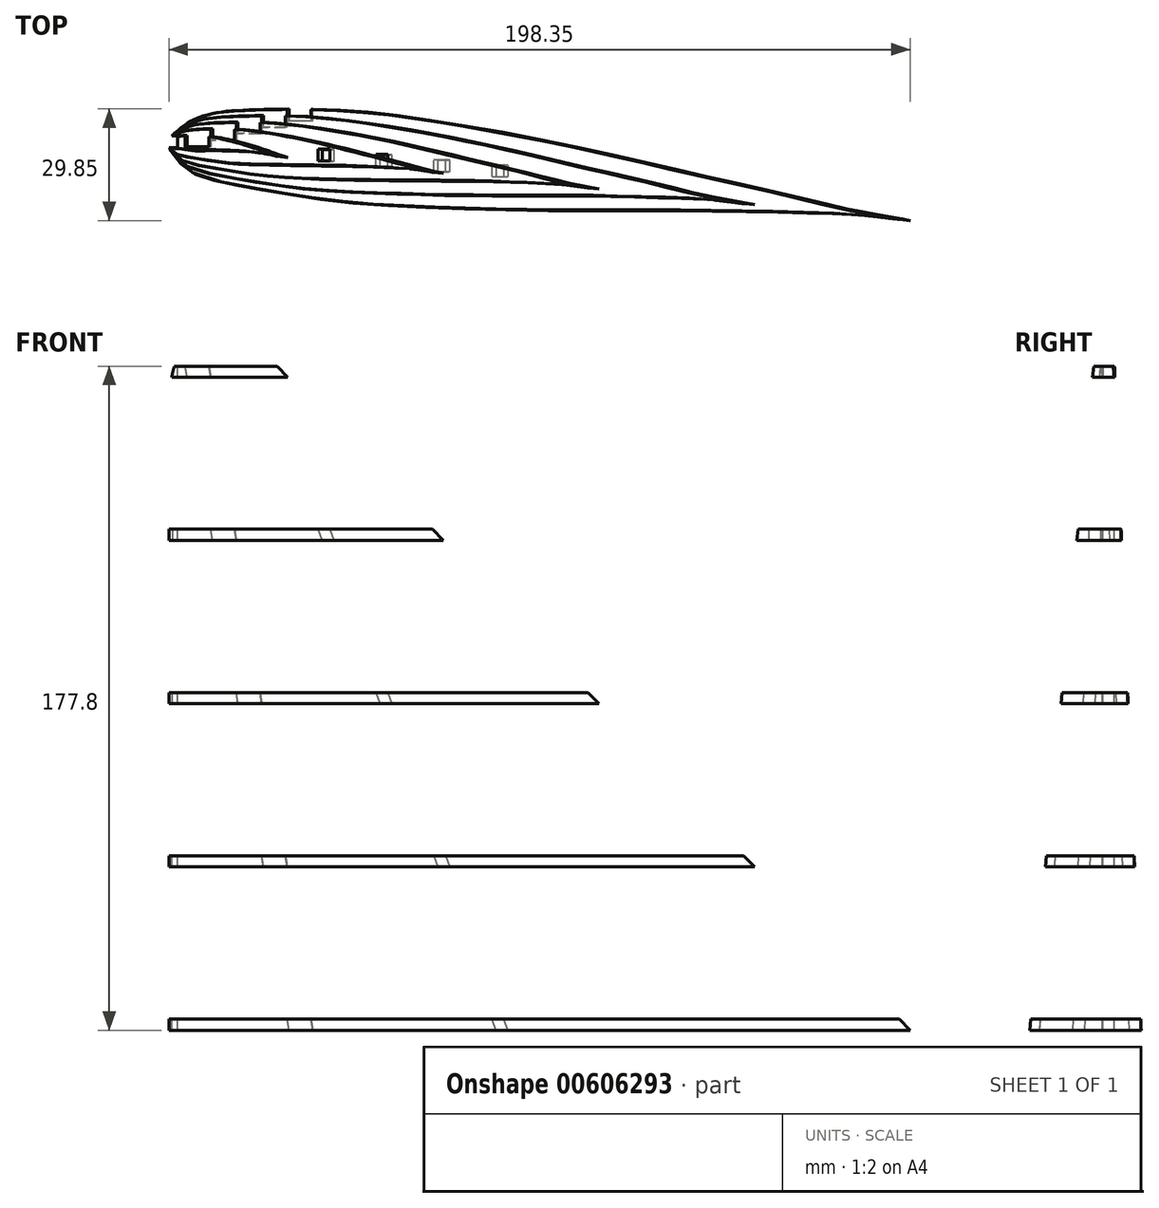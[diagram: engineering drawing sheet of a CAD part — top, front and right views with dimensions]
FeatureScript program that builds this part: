
annotation { "Feature Type Name" : "Feature", "Feature Type Description" : "" }
export const myFeature = defineFeature(function(context is Context, id is Id, definition is map)
    precondition{}
    {
        {
            var Q0;
            Q0=qCreatedBy(makeId("Top.planeOp"),FACE);
            var sketch = newSketch(context, id + "F0", { "sketchPlane" : qUnion([Q0])});
            skLineSegment(sketch, "E0", {"start": v(0, 0) * mm, "end": v(2.33, 2.26) * mm});
            skLineSegment(sketch, "E1", {"start": v(2.33, 2.26) * mm, "end": v(3.53, 3.33) * mm});
            skLineSegment(sketch, "E2", {"start": v(3.53, 3.33) * mm, "end": v(4.77, 4.31) * mm});
            skLineSegment(sketch, "E3", {"start": v(4.77, 4.31) * mm, "end": v(6.35, 5.36) * mm});
            skLineSegment(sketch, "E4", {"start": v(6.35, 5.36) * mm, "end": v(7.43, 5.94) * mm});
            skLineSegment(sketch, "E5", {"start": v(7.43, 5.94) * mm, "end": v(8.86, 6.56) * mm});
            skLineSegment(sketch, "E6", {"start": v(8.86, 6.56) * mm, "end": v(10.34, 7.07) * mm});
            skLineSegment(sketch, "E7", {"start": v(10.34, 7.07) * mm, "end": v(11.88, 7.48) * mm});
            skLineSegment(sketch, "E8", {"start": v(11.88, 7.48) * mm, "end": v(13.45, 7.8) * mm});
            skLineSegment(sketch, "E9", {"start": v(13.45, 7.8) * mm, "end": v(16.68, 8.22) * mm});
            skLineSegment(sketch, "E10", {"start": v(16.68, 8.22) * mm, "end": v(19.98, 8.45) * mm});
            skLineSegment(sketch, "E11", {"start": v(19.98, 8.45) * mm, "end": v(22.04, 8.54) * mm});
            skLineSegment(sketch, "E12", {"start": v(22.04, 8.54) * mm, "end": v(29.75, 8.77) * mm});
            skLineSegment(sketch, "E13", {"start": v(29.75, 8.77) * mm, "end": v(36.12, 8.82) * mm});
            skLineSegment(sketch, "E14", {"start": v(36.12, 8.82) * mm, "end": v(42.43, 8.7) * mm});
            skLineSegment(sketch, "E15", {"start": v(42.43, 8.7) * mm, "end": v(46.07, 8.54) * mm});
            skLineSegment(sketch, "E16", {"start": v(46.07, 8.54) * mm, "end": v(55.05, 7.84) * mm});
            skLineSegment(sketch, "E17", {"start": v(55.05, 7.84) * mm, "end": v(61.4, 7.12) * mm});
            skLineSegment(sketch, "E18", {"start": v(61.4, 7.12) * mm, "end": v(67.74, 6.27) * mm});
            skLineSegment(sketch, "E19", {"start": v(67.74, 6.27) * mm, "end": v(76.25, 4.96) * mm});
            skLineSegment(sketch, "E20", {"start": v(76.25, 4.96) * mm, "end": v(86.73, 3.2) * mm});
            skLineSegment(sketch, "E21", {"start": v(86.73, 3.2) * mm, "end": v(99.29, 0.84) * mm});
            skLineSegment(sketch, "E22", {"start": v(99.29, 0.84) * mm, "end": v(109.21, -1.2) * mm});
            skLineSegment(sketch, "E23", {"start": v(109.21, -1.2) * mm, "end": v(123.98, -4.49) * mm});
            skLineSegment(sketch, "E24", {"start": v(123.98, -4.49) * mm, "end": v(130.17, -5.92) * mm});
            skLineSegment(sketch, "E25", {"start": v(130.17, -5.92) * mm, "end": v(136.44, -7.38) * mm});
            skLineSegment(sketch, "E26", {"start": v(136.44, -7.38) * mm, "end": v(142.37, -8.74) * mm});
            skLineSegment(sketch, "E27", {"start": v(142.37, -8.74) * mm, "end": v(149.34, -10.3) * mm});
            skLineSegment(sketch, "E28", {"start": v(149.34, -10.3) * mm, "end": v(155.82, -11.75) * mm});
            skLineSegment(sketch, "E29", {"start": v(155.82, -11.75) * mm, "end": v(162.12, -13.17) * mm});
            skLineSegment(sketch, "E30", {"start": v(162.12, -13.17) * mm, "end": v(165.14, -13.87) * mm});
            skLineSegment(sketch, "E31", {"start": v(165.14, -13.87) * mm, "end": v(168.06, -14.55) * mm});
            skLineSegment(sketch, "E32", {"start": v(168.06, -14.55) * mm, "end": v(171.17, -15.29) * mm});
            skLineSegment(sketch, "E33", {"start": v(171.17, -15.29) * mm, "end": v(173.51, -15.86) * mm});
            skLineSegment(sketch, "E34", {"start": v(173.51, -15.86) * mm, "end": v(176.14, -16.5) * mm});
            skLineSegment(sketch, "E35", {"start": v(176.14, -16.5) * mm, "end": v(178.86, -17.16) * mm});
            skLineSegment(sketch, "E36", {"start": v(178.86, -17.16) * mm, "end": v(181.8, -17.82) * mm});
            skLineSegment(sketch, "E37", {"start": v(181.8, -17.82) * mm, "end": v(183.4, -18.16) * mm});
            skLineSegment(sketch, "E38", {"start": v(183.4, -18.16) * mm, "end": v(185.1, -18.5) * mm});
            skLineSegment(sketch, "E39", {"start": v(185.1, -18.5) * mm, "end": v(186.92, -18.87) * mm});
            skLineSegment(sketch, "E40", {"start": v(186.92, -18.87) * mm, "end": v(188.88, -19.24) * mm});
            skLineSegment(sketch, "E41", {"start": v(188.88, -19.24) * mm, "end": v(191.22, -19.66) * mm});
            skLineSegment(sketch, "E42", {"start": v(191.22, -19.66) * mm, "end": v(193.25, -20.01) * mm});
            skLineSegment(sketch, "E43", {"start": v(193.25, -20.01) * mm, "end": v(195.45, -20.38) * mm});
            skLineSegment(sketch, "E44", {"start": v(195.45, -20.38) * mm, "end": v(196.45, -20.55) * mm});
            skLineSegment(sketch, "E45", {"start": v(196.45, -20.55) * mm, "end": v(197.34, -20.7) * mm});
            skLineSegment(sketch, "E46", {"start": v(197.34, -20.7) * mm, "end": v(198.1, -20.83) * mm});
            skLineSegment(sketch, "E47", {"start": v(198.1, -20.83) * mm, "end": v(198.67, -20.94) * mm});
            skLineSegment(sketch, "E48", {"start": v(198.67, -20.94) * mm, "end": v(199.04, -21) * mm});
            skLineSegment(sketch, "E49", {"start": v(199.04, -21) * mm, "end": v(199.17, -21.05) * mm});
            skLineSegment(sketch, "E50", {"start": v(199.17, -21.05) * mm, "end": v(199.05, -21.04) * mm});
            skLineSegment(sketch, "E51", {"start": v(199.05, -21.04) * mm, "end": v(198.67, -21) * mm});
            skLineSegment(sketch, "E52", {"start": v(198.67, -21) * mm, "end": v(198.08, -20.93) * mm});
            skLineSegment(sketch, "E53", {"start": v(198.08, -20.93) * mm, "end": v(197.31, -20.84) * mm});
            skLineSegment(sketch, "E54", {"start": v(197.31, -20.84) * mm, "end": v(196.4, -20.72) * mm});
            skLineSegment(sketch, "E55", {"start": v(196.4, -20.72) * mm, "end": v(195.4, -20.6) * mm});
            skLineSegment(sketch, "E56", {"start": v(195.4, -20.6) * mm, "end": v(192.61, -20.25) * mm});
            skLineSegment(sketch, "E57", {"start": v(192.61, -20.25) * mm, "end": v(191.14, -20.09) * mm});
            skLineSegment(sketch, "E58", {"start": v(191.14, -20.09) * mm, "end": v(189.16, -19.88) * mm});
            skLineSegment(sketch, "E59", {"start": v(189.16, -19.88) * mm, "end": v(187.3, -19.7) * mm});
            skLineSegment(sketch, "E60", {"start": v(187.3, -19.7) * mm, "end": v(185.56, -19.56) * mm});
            skLineSegment(sketch, "E61", {"start": v(185.56, -19.56) * mm, "end": v(183.9, -19.44) * mm});
            skLineSegment(sketch, "E62", {"start": v(183.9, -19.44) * mm, "end": v(182.34, -19.35) * mm});
            skLineSegment(sketch, "E63", {"start": v(182.34, -19.35) * mm, "end": v(179.38, -19.22) * mm});
            skLineSegment(sketch, "E64", {"start": v(179.38, -19.22) * mm, "end": v(172.56, -19.06) * mm});
            skLineSegment(sketch, "E65", {"start": v(172.56, -19.06) * mm, "end": v(170.97, -19.03) * mm});
            skLineSegment(sketch, "E66", {"start": v(170.97, -19.03) * mm, "end": v(168, -18.97) * mm});
            skLineSegment(sketch, "E67", {"start": v(168, -18.97) * mm, "end": v(164.94, -18.9) * mm});
            skLineSegment(sketch, "E68", {"start": v(164.94, -18.9) * mm, "end": v(161.8, -18.83) * mm});
            skLineSegment(sketch, "E69", {"start": v(161.8, -18.83) * mm, "end": v(155.31, -18.68) * mm});
            skLineSegment(sketch, "E70", {"start": v(155.31, -18.68) * mm, "end": v(148.7, -18.55) * mm});
            skLineSegment(sketch, "E71", {"start": v(148.7, -18.55) * mm, "end": v(142.57, -18.47) * mm});
            skLineSegment(sketch, "E72", {"start": v(142.57, -18.47) * mm, "end": v(135.55, -18.43) * mm});
            skLineSegment(sketch, "E73", {"start": v(135.55, -18.43) * mm, "end": v(122.78, -18.45) * mm});
            skLineSegment(sketch, "E74", {"start": v(122.78, -18.45) * mm, "end": v(107.63, -18.47) * mm});
            skLineSegment(sketch, "E75", {"start": v(107.63, -18.47) * mm, "end": v(97.5, -18.36) * mm});
            skLineSegment(sketch, "E76", {"start": v(97.5, -18.36) * mm, "end": v(84.74, -18.06) * mm});
            skLineSegment(sketch, "E77", {"start": v(84.74, -18.06) * mm, "end": v(72.88, -17.67) * mm});
            skLineSegment(sketch, "E78", {"start": v(72.88, -17.67) * mm, "end": v(59.08, -17.03) * mm});
            skLineSegment(sketch, "E79", {"start": v(59.08, -17.03) * mm, "end": v(52.7, -16.59) * mm});
            skLineSegment(sketch, "E80", {"start": v(52.7, -16.59) * mm, "end": v(46.4, -16) * mm});
            skLineSegment(sketch, "E81", {"start": v(46.4, -16) * mm, "end": v(42.1, -15.49) * mm});
            skLineSegment(sketch, "E82", {"start": v(42.1, -15.49) * mm, "end": v(33.97, -14.26) * mm});
            skLineSegment(sketch, "E83", {"start": v(33.97, -14.26) * mm, "end": v(27.74, -13.17) * mm});
            skLineSegment(sketch, "E84", {"start": v(27.74, -13.17) * mm, "end": v(18.67, -11.52) * mm});
            skLineSegment(sketch, "E85", {"start": v(18.67, -11.52) * mm, "end": v(14.77, -10.79) * mm});
            skLineSegment(sketch, "E86", {"start": v(14.77, -10.79) * mm, "end": v(11.53, -10) * mm});
            skLineSegment(sketch, "E87", {"start": v(11.53, -10) * mm, "end": v(9.97, -9.52) * mm});
            skLineSegment(sketch, "E88", {"start": v(9.97, -9.52) * mm, "end": v(8.48, -8.94) * mm});
            skLineSegment(sketch, "E89", {"start": v(8.48, -8.94) * mm, "end": v(7.07, -8.26) * mm});
            skLineSegment(sketch, "E90", {"start": v(7.07, -8.26) * mm, "end": v(5.75, -7.45) * mm});
            skLineSegment(sketch, "E91", {"start": v(5.75, -7.45) * mm, "end": v(4.17, -6.16) * mm});
            skLineSegment(sketch, "E92", {"start": v(4.17, -6.16) * mm, "end": v(3.47, -5.41) * mm});
            skLineSegment(sketch, "E93", {"start": v(3.47, -5.41) * mm, "end": v(2.5, -4.18) * mm});
            skLineSegment(sketch, "E94", {"start": v(2.5, -4.18) * mm, "end": v(1.62, -2.84) * mm});
            skLineSegment(sketch, "E95", {"start": v(1.62, -2.84) * mm, "end": v(0, 0) * mm});
            skSolve(sketch);
        }
        {
            var Q0;
            Q0=qCreatedBy(makeId("Top.planeOp"),FACE);
            var sketch = newSketch(context, id + "F1", { "sketchPlane" : qUnion([Q0])});
            skPoint(sketch, "E96.0", {"position": v(0, 0) * mm});
            skPoint(sketch, "E96.1", {"position": v(3.53, 3.33) * mm});
            skPoint(sketch, "E96.2", {"position": v(7.43, 5.94) * mm});
            skPoint(sketch, "E96.3", {"position": v(13.45, 7.8) * mm});
            skPoint(sketch, "E96.4", {"position": v(22.04, 8.54) * mm});
            skPoint(sketch, "E96.5", {"position": v(42.43, 8.7) * mm});
            skPoint(sketch, "E96.6", {"position": v(67.74, 6.27) * mm});
            skPoint(sketch, "E96.7", {"position": v(109.21, -1.2) * mm});
            skPoint(sketch, "E96.8", {"position": v(142.37, -8.74) * mm});
            skPoint(sketch, "E96.9", {"position": v(165.14, -13.87) * mm});
            skPoint(sketch, "E96.10", {"position": v(178.86, -17.16) * mm});
            skPoint(sketch, "E96.11", {"position": v(186.92, -18.87) * mm});
            skPoint(sketch, "E96.12", {"position": v(193.25, -20.01) * mm});
            skPoint(sketch, "E96.13", {"position": v(197.34, -20.7) * mm});
            skPoint(sketch, "E96.14", {"position": v(199.17, -21.05) * mm});
            skPoint(sketch, "E97.0", {"position": v(2.5, -4.18) * mm});
            skPoint(sketch, "E97.1", {"position": v(7.07, -8.26) * mm});
            skPoint(sketch, "E97.2", {"position": v(14.77, -10.79) * mm});
            skPoint(sketch, "E97.3", {"position": v(27.74, -13.17) * mm});
            skPoint(sketch, "E97.4", {"position": v(46.4, -16) * mm});
            skPoint(sketch, "E97.5", {"position": v(72.88, -17.67) * mm});
            skPoint(sketch, "E97.6", {"position": v(107.63, -18.47) * mm});
            skPoint(sketch, "E97.7", {"position": v(142.57, -18.47) * mm});
            skPoint(sketch, "E97.8", {"position": v(164.94, -18.9) * mm});
            skPoint(sketch, "E97.9", {"position": v(179.38, -19.22) * mm});
            skPoint(sketch, "E97.10", {"position": v(185.56, -19.56) * mm});
            skPoint(sketch, "E97.11", {"position": v(191.14, -20.09) * mm});
            skPoint(sketch, "E97.12", {"position": v(195.4, -20.6) * mm});
            skFitSpline(sketch, "E98", {"points": [v(0, 0) * mm, v(3.53, 3.33) * mm, v(7.43, 5.94) * mm, v(13.45, 7.8) * mm, v(22.04, 8.54) * mm, v(42.43, 8.7) * mm, v(67.74, 6.27) * mm, v(109.21, -1.2) * mm, v(142.37, -8.74) * mm, v(165.14, -13.87) * mm, v(178.86, -17.16) * mm, v(186.92, -18.87) * mm, v(193.25, -20.01) * mm, v(197.34, -20.7) * mm, v(199.17, -21.05) * mm], "startDerivative": vector(77.94, 76.97) * mm, "endDerivative": vector(59.78, -11.65) * mm});
            skFitSpline(sketch, "E99", {"points": [v(0, 0) * mm, v(2.5, -4.18) * mm, v(7.07, -8.26) * mm, v(14.77, -10.79) * mm, v(27.74, -13.17) * mm, v(46.4, -16) * mm, v(72.88, -17.67) * mm, v(107.63, -18.47) * mm, v(142.57, -18.47) * mm, v(164.94, -18.9) * mm, v(179.38, -19.22) * mm, v(185.56, -19.56) * mm, v(191.14, -20.09) * mm, v(195.4, -20.6) * mm, v(199.17, -21.05) * mm], "startDerivative": vector(49.75, -95.35) * mm, "endDerivative": vector(95.8, -11.43) * mm});
            skSolve(sketch);
        }
        {
            var Q0;
            Q0=qCreatedBy(makeId("Top.planeOp"),FACE);
            cPlane(context, id + "F2", {"entities" : qUnion([Q0]), "cplaneType" : CPlaneType.OFFSET, "offset" : 177.8 * mm, "width" : 152.4 * mm, "height" : 152.4 * mm});
        }
        {
            var Q0;
            Q0=qCreatedBy(id+"F2.planeOp",FACE);
            var sketch = newSketch(context, id + "F3", { "sketchPlane" : qUnion([Q0])});
            skLineSegment(sketch, "E100", {"start": v(0, 0) * mm, "end": v(0.76, 0.6) * mm});
            skLineSegment(sketch, "E101", {"start": v(0.76, 0.6) * mm, "end": v(1.2, 0.87) * mm});
            skLineSegment(sketch, "E102", {"start": v(1.2, 0.87) * mm, "end": v(1.6, 1.06) * mm});
            skLineSegment(sketch, "E103", {"start": v(1.6, 1.06) * mm, "end": v(2.51, 1.33) * mm});
            skLineSegment(sketch, "E104", {"start": v(2.51, 1.33) * mm, "end": v(3.73, 1.52) * mm});
            skLineSegment(sketch, "E105", {"start": v(3.73, 1.52) * mm, "end": v(5.41, 1.66) * mm});
            skLineSegment(sketch, "E106", {"start": v(5.41, 1.66) * mm, "end": v(7.35, 1.7) * mm});
            skLineSegment(sketch, "E107", {"start": v(7.35, 1.7) * mm, "end": v(9.24, 1.62) * mm});
            skLineSegment(sketch, "E108", {"start": v(9.24, 1.62) * mm, "end": v(11.74, 1.34) * mm});
            skLineSegment(sketch, "E109", {"start": v(11.74, 1.34) * mm, "end": v(13.07, 1.13) * mm});
            skLineSegment(sketch, "E110", {"start": v(13.07, 1.13) * mm, "end": v(16.43, 0.42) * mm});
            skLineSegment(sketch, "E111", {"start": v(16.43, 0.42) * mm, "end": v(18.66, -0.16) * mm});
            skLineSegment(sketch, "E112", {"start": v(18.66, -0.16) * mm, "end": v(21.09, -0.87) * mm});
            skLineSegment(sketch, "E113", {"start": v(21.09, -0.87) * mm, "end": v(22.44, -1.3) * mm});
            skLineSegment(sketch, "E114", {"start": v(22.44, -1.3) * mm, "end": v(24.3, -1.92) * mm});
            skLineSegment(sketch, "E115", {"start": v(24.3, -1.92) * mm, "end": v(25.2, -2.24) * mm});
            skLineSegment(sketch, "E116", {"start": v(25.2, -2.24) * mm, "end": v(25.86, -2.48) * mm});
            skLineSegment(sketch, "E117", {"start": v(25.86, -2.48) * mm, "end": v(26.64, -2.77) * mm});
            skLineSegment(sketch, "E118", {"start": v(26.64, -2.77) * mm, "end": v(27.1, -2.93) * mm});
            skLineSegment(sketch, "E119", {"start": v(27.1, -2.93) * mm, "end": v(27.64, -3.13) * mm});
            skLineSegment(sketch, "E120", {"start": v(27.64, -3.13) * mm, "end": v(28.26, -3.35) * mm});
            skLineSegment(sketch, "E121", {"start": v(28.26, -3.35) * mm, "end": v(28.99, -3.6) * mm});
            skLineSegment(sketch, "E122", {"start": v(28.99, -3.6) * mm, "end": v(29.3, -3.71) * mm});
            skLineSegment(sketch, "E123", {"start": v(29.3, -3.71) * mm, "end": v(29.57, -3.8) * mm});
            skLineSegment(sketch, "E124", {"start": v(29.57, -3.8) * mm, "end": v(29.74, -3.87) * mm});
            skLineSegment(sketch, "E125", {"start": v(29.74, -3.87) * mm, "end": v(29.79, -3.9) * mm});
            skLineSegment(sketch, "E126", {"start": v(29.79, -3.9) * mm, "end": v(29.75, -3.88) * mm});
            skLineSegment(sketch, "E127", {"start": v(29.75, -3.88) * mm, "end": v(29.24, -3.73) * mm});
            skLineSegment(sketch, "E128", {"start": v(29.24, -3.73) * mm, "end": v(28.9, -3.64) * mm});
            skLineSegment(sketch, "E129", {"start": v(28.9, -3.64) * mm, "end": v(27.91, -3.4) * mm});
            skLineSegment(sketch, "E130", {"start": v(27.91, -3.4) * mm, "end": v(26.5, -3.14) * mm});
            skLineSegment(sketch, "E131", {"start": v(26.5, -3.14) * mm, "end": v(24.27, -2.81) * mm});
            skLineSegment(sketch, "E132", {"start": v(24.27, -2.81) * mm, "end": v(21.92, -2.54) * mm});
            skLineSegment(sketch, "E133", {"start": v(21.92, -2.54) * mm, "end": v(20.37, -2.4) * mm});
            skLineSegment(sketch, "E134", {"start": v(20.37, -2.4) * mm, "end": v(18.46, -2.28) * mm});
            skLineSegment(sketch, "E135", {"start": v(18.46, -2.28) * mm, "end": v(16.3, -2.18) * mm});
            skLineSegment(sketch, "E136", {"start": v(16.3, -2.18) * mm, "end": v(10.72, -2.1) * mm});
            skLineSegment(sketch, "E137", {"start": v(10.72, -2.1) * mm, "end": v(8.83, -2.14) * mm});
            skLineSegment(sketch, "E138", {"start": v(8.83, -2.14) * mm, "end": v(6.9, -2.15) * mm});
            skLineSegment(sketch, "E139", {"start": v(6.9, -2.15) * mm, "end": v(5.88, -2.1) * mm});
            skLineSegment(sketch, "E140", {"start": v(5.88, -2.1) * mm, "end": v(5.05, -2) * mm});
            skLineSegment(sketch, "E141", {"start": v(5.05, -2) * mm, "end": v(3.17, -1.7) * mm});
            skLineSegment(sketch, "E142", {"start": v(3.17, -1.7) * mm, "end": v(2.33, -1.58) * mm});
            skLineSegment(sketch, "E143", {"start": v(2.33, -1.58) * mm, "end": v(1.12, -1.37) * mm});
            skLineSegment(sketch, "E144", {"start": v(1.12, -1.37) * mm, "end": v(0.69, -1.18) * mm});
            skLineSegment(sketch, "E145", {"start": v(0.69, -1.18) * mm, "end": v(0.36, -0.9) * mm});
            skLineSegment(sketch, "E146", {"start": v(0.36, -0.9) * mm, "end": v(0.14, -0.48) * mm});
            skLineSegment(sketch, "E147", {"start": v(0.14, -0.48) * mm, "end": v(0, 0) * mm});
            skSolve(sketch);
        }
        {
            var Q0;
            Q0=qCreatedBy(id+"F2.planeOp",FACE);
            var sketch = newSketch(context, id + "F4", { "sketchPlane" : qUnion([Q0])});
            skPoint(sketch, "E148.0", {"position": v(0, 0) * mm});
            skPoint(sketch, "E148.1", {"position": v(1.2, 0.87) * mm});
            skPoint(sketch, "E148.2", {"position": v(3.73, 1.52) * mm});
            skPoint(sketch, "E148.3", {"position": v(7.35, 1.7) * mm});
            skPoint(sketch, "E148.4", {"position": v(13.07, 1.13) * mm});
            skPoint(sketch, "E148.5", {"position": v(21.09, -0.87) * mm});
            skPoint(sketch, "E148.6", {"position": v(24.3, -1.92) * mm});
            skPoint(sketch, "E148.7", {"position": v(26.64, -2.77) * mm});
            skPoint(sketch, "E148.8", {"position": v(28.26, -3.35) * mm});
            skPoint(sketch, "E148.9", {"position": v(29.3, -3.71) * mm});
            skPoint(sketch, "E148.10", {"position": v(29.79, -3.9) * mm});
            skPoint(sketch, "E148.11", {"position": v(28.9, -3.64) * mm});
            skPoint(sketch, "E148.12", {"position": v(27.91, -3.4) * mm});
            skPoint(sketch, "E148.13", {"position": v(24.27, -2.81) * mm});
            skPoint(sketch, "E148.14", {"position": v(20.37, -2.4) * mm});
            skPoint(sketch, "E148.15", {"position": v(10.72, -2.1) * mm});
            skPoint(sketch, "E148.16", {"position": v(6.9, -2.15) * mm});
            skPoint(sketch, "E148.17", {"position": v(3.17, -1.7) * mm});
            skPoint(sketch, "E148.18", {"position": v(1.12, -1.37) * mm});
            skPoint(sketch, "E148.19", {"position": v(0.36, -0.9) * mm});
            skFitSpline(sketch, "E149", {"points": [v(0, 0) * mm, v(1.2, 0.87) * mm, v(3.73, 1.52) * mm, v(7.35, 1.7) * mm, v(13.07, 1.13) * mm, v(21.09, -0.87) * mm, v(24.3, -1.92) * mm, v(26.64, -2.77) * mm, v(28.26, -3.35) * mm, v(29.3, -3.71) * mm, v(29.79, -3.9) * mm], "startDerivative": vector(14.25, 12.7) * mm, "endDerivative": vector(10.02, -3.8) * mm});
            skFitSpline(sketch, "E150", {"points": [v(0, 0) * mm, v(0.36, -0.9) * mm, v(1.12, -1.37) * mm, v(3.17, -1.7) * mm, v(6.9, -2.15) * mm, v(10.72, -2.1) * mm, v(20.37, -2.4) * mm, v(24.27, -2.81) * mm, v(27.91, -3.4) * mm, v(28.9, -3.64) * mm, v(29.79, -3.9) * mm], "startDerivative": vector(4.45, -16.35) * mm, "endDerivative": vector(15.54, -4.48) * mm});
            skSolve(sketch);
        }
        {
            var Q0;
            Q0=makeQuery(id+"F4.imprint","IMPRINT",FACE,{"disambiguationData":[TD([[makeQuery(id+"F4.imprint","IMPRINT",EDGE,{"derivedFrom":sQuery(id+"F4.wireOp",EDGE,"E149")}),-1.0]])]});
            var Q1;
            Q1=makeQuery(id+"F1.imprint","IMPRINT",FACE,{"disambiguationData":[TD([[makeQuery(id+"F1.imprint","IMPRINT",EDGE,{"derivedFrom":sQuery(id+"F1.wireOp",EDGE,"E98")}),-1.0]])]});
            loft(context, id + "F5", {"sheetProfilesArray" : [{ "sheetProfileEntities" : qUnion([Q0]) }, { "sheetProfileEntities" : qUnion([Q1]) }]});
        }
        {
            var Q0;
            Q0=qCreatedBy(makeId("Front.planeOp"),FACE);
            var sketch = newSketch(context, id + "F6", { "sketchPlane" : qUnion([Q0])});
            skLineSegment(sketch, "E151", {"start": v(0, 0) * mm, "end": v(0, 3) * mm, "construction": true});
            skLineSegment(sketch, "E152.bottom", {"start": v(0, 3) * mm, "end": v(229.07, 3) * mm});
            skLineSegment(sketch, "E152.top", {"start": v(0, 43.7) * mm, "end": v(229.07, 43.7) * mm});
            skLineSegment(sketch, "E152.left", {"start": v(0, 3) * mm, "end": v(0, 43.7) * mm});
            skLineSegment(sketch, "E152.right", {"start": v(229.07, 3) * mm, "end": v(229.07, 43.7) * mm});
            skLineSegment(sketch, "E153.0.1.0", {"start": v(229.07, 46.71) * mm, "end": v(229.07, 87.42) * mm});
            skLineSegment(sketch, "E153.0.1.1", {"start": v(0, 46.71) * mm, "end": v(0, 87.42) * mm});
            skLineSegment(sketch, "E153.0.1.2", {"start": v(0, 87.42) * mm, "end": v(229.07, 87.42) * mm});
            skLineSegment(sketch, "E153.0.1.3", {"start": v(0, 46.71) * mm, "end": v(229.07, 46.71) * mm});
            skLineSegment(sketch, "E153.0.1.4", {"start": v(0, 43.71) * mm, "end": v(0, 46.71) * mm, "construction": true});
            skLineSegment(sketch, "E153.0.2.0", {"start": v(229.07, 90.43) * mm, "end": v(229.07, 131.13) * mm});
            skLineSegment(sketch, "E153.0.2.1", {"start": v(0, 90.43) * mm, "end": v(0, 131.13) * mm});
            skLineSegment(sketch, "E153.0.2.2", {"start": v(0, 131.13) * mm, "end": v(229.07, 131.13) * mm});
            skLineSegment(sketch, "E153.0.2.3", {"start": v(0, 90.43) * mm, "end": v(229.07, 90.43) * mm});
            skLineSegment(sketch, "E153.0.2.4", {"start": v(0, 87.43) * mm, "end": v(0, 90.43) * mm, "construction": true});
            skLineSegment(sketch, "E153.0.3.0", {"start": v(229.07, 134.14) * mm, "end": v(229.07, 174.84) * mm});
            skLineSegment(sketch, "E153.0.3.1", {"start": v(0, 134.14) * mm, "end": v(0, 174.84) * mm});
            skLineSegment(sketch, "E153.0.3.2", {"start": v(0, 174.84) * mm, "end": v(229.07, 174.84) * mm});
            skLineSegment(sketch, "E153.0.3.3", {"start": v(0, 134.14) * mm, "end": v(229.07, 134.14) * mm});
            skLineSegment(sketch, "E153.0.3.4", {"start": v(0, 131.14) * mm, "end": v(0, 134.14) * mm, "construction": true});
            skLineSegment(sketch, "E153.direction1", {"start": v(0, 0) * mm, "end": v(25.4, 0) * mm, "construction": true});
            skLineSegment(sketch, "E153.direction2", {"start": v(0, 0) * mm, "end": v(0, 43.71) * mm, "construction": true});
            skSolve(sketch);
        }
        {
            var Q0;
            Q0=makeQuery(id+"F6.imprint","IMPRINT",FACE,{"disambiguationData":[TD([[makeQuery(id+"F6.imprint","IMPRINT",EDGE,{"derivedFrom":sQuery(id+"F6.wireOp",EDGE,"E152.bottom")}),1.0]])]});
            var Q1;
            Q1=makeQuery(id+"F6.imprint","IMPRINT",FACE,{"disambiguationData":[TD([[makeQuery(id+"F6.imprint","IMPRINT",EDGE,{"derivedFrom":sQuery(id+"F6.wireOp",EDGE,"E153.0.1.0")}),1.0]])]});
            var Q2;
            Q2=makeQuery(id+"F6.imprint","IMPRINT",FACE,{"disambiguationData":[TD([[makeQuery(id+"F6.imprint","IMPRINT",EDGE,{"derivedFrom":sQuery(id+"F6.wireOp",EDGE,"E153.0.2.0")}),1.0]])]});
            var Q3;
            Q3=makeQuery(id+"F6.imprint","IMPRINT",FACE,{"disambiguationData":[TD([[makeQuery(id+"F6.imprint","IMPRINT",EDGE,{"derivedFrom":sQuery(id+"F6.wireOp",EDGE,"E153.0.3.0")}),1.0]])]});
            extrude(context, id + "F7", {"entities" : qUnion([Q0, Q1, Q2, Q3]), "operationType" : NewBodyOperationType.REMOVE, "oppositeDirection" : true, "depth" : 127 * mm, "offsetDistance" : 25.4 * mm, "hasSecondDirection" : true, "secondDirectionOppositeDirection" : false, "secondDirectionDepth" : 127 * mm});
        }
        {
            var Q0;
            Q0=makeQuery(id+"F3.imprint","IMPRINT",FACE,{"disambiguationData":[TD([[makeQuery(id+"F3.imprint","IMPRINT",EDGE,{"derivedFrom":sQuery(id+"F3.wireOp",EDGE,"E100")}),-1.0]])]});
            var sketch = newSketch(context, id + "F8", { "sketchPlane" : qUnion([Q0])});
            skLineSegment(sketch, "E154", {"start": v(0, 0) * mm, "end": v(3.17, 0) * mm, "construction": true});
            skLineSegment(sketch, "E155", {"start": v(3.17, 0) * mm, "end": v(3.17, 1.59) * mm});
            skLineSegment(sketch, "E156", {"start": v(3.17, 0) * mm, "end": v(3.17, -1.59) * mm});
            skLineSegment(sketch, "E157", {"start": v(3.17, -1.59) * mm, "end": v(0, -1.59) * mm});
            skLineSegment(sketch, "E158", {"start": v(0, -1.59) * mm, "end": v(0, 1.59) * mm});
            skLineSegment(sketch, "E159", {"start": v(0, 1.59) * mm, "end": v(3.18, 1.59) * mm});
            skSolve(sketch);
        }
        {
            var Q0;
            {var subQ4=makeQuery(id+"F3.imprint","IMPRINT",EDGE,{"derivedFrom":sQuery(id+"F3.wireOp",EDGE,"E143")});Q0=makeQuery(id+"F8.imprint","IMPRINT",FACE,{"disambiguationData":[TD([[makeQuery(id+"F8.imprint","IMPRINT",EDGE,{"derivedFrom":subQ4}),1.0]])]});}
            var Q1;
            {var subQ2=sQuery(id+"F8.wireOp",EDGE,"E156");Q1=makeQuery(id+"F8.imprint","IMPRINT",FACE,{"disambiguationData":[TD([[makeQuery(id+"F8.imprint","IMPRINT",EDGE,{"derivedFrom":subQ2}),-1.0]])]});}
            var Q2;
            {var subQ1=sQuery(id+"F8.wireOp",EDGE,"E159");Q2=makeQuery(id+"F8.imprint","IMPRINT",FACE,{"disambiguationData":[TD([[makeQuery(id+"F8.imprint","IMPRINT",EDGE,{"derivedFrom":subQ1}),-1.0]])]});}
            extrude(context, id + "F9", {"entities" : qUnion([Q0, Q1, Q2]), "operationType" : NewBodyOperationType.REMOVE, "oppositeDirection" : true, "depth" : 508 * mm, "offsetDistance" : 25.4 * mm});
        }
        {
            var Q0;
            Q0=makeQuery(id+"F0.imprint","IMPRINT",FACE,{"disambiguationData":[TD([[makeQuery(id+"F0.imprint","IMPRINT",EDGE,{"derivedFrom":sQuery(id+"F0.wireOp",EDGE,"E0")}),-1.0]])]});
            var sketch = newSketch(context, id + "F10", { "sketchPlane" : qUnion([Q0])});
            skPoint(sketch, "E160.0", {"position": v(36.12, 8.82) * mm});
            skLineSegment(sketch, "E161", {"start": v(39.3, 5.65) * mm, "end": v(39.3, 8.82) * mm});
            skLineSegment(sketch, "E162", {"start": v(39.3, 8.82) * mm, "end": v(32.94, 8.82) * mm});
            skLineSegment(sketch, "E163", {"start": v(32.94, 8.82) * mm, "end": v(32.94, 5.65) * mm});
            skLineSegment(sketch, "E164", {"start": v(32.94, 5.65) * mm, "end": v(39.3, 5.65) * mm});
            skSolve(sketch);
        }
        {
            var Q0;
            Q0=makeQuery(id+"F3.imprint","IMPRINT",FACE,{"disambiguationData":[TD([[makeQuery(id+"F3.imprint","IMPRINT",EDGE,{"derivedFrom":sQuery(id+"F3.wireOp",EDGE,"E100")}),-1.0]])]});
            var sketch = newSketch(context, id + "F11", { "sketchPlane" : qUnion([Q0])});
            skFitSpline(sketch, "E165.0", {"points": [v(32.6, -4.18) * mm, v(32, -3.96) * mm, v(30.8, -3.58) * mm, v(29.02, -2.96) * mm, v(27.24, -2.33) * mm, v(25.44, -1.72) * mm, v(23.64, -1.16) * mm, v(21.21, -0.46) * mm, v(18.77, 0.19) * mm, v(16.32, 0.76) * mm, v(13.86, 1.27) * mm, v(11.37, 1.63) * mm, v(8.87, 1.8) * mm, v(6.97, 1.84) * mm, v(5.06, 1.77) * mm, v(3.8, 1.63) * mm, v(3.18, 1.51) * mm], "construction": true});
            skLineSegment(sketch, "E166", {"start": v(5.21, -1.37) * mm, "end": v(5.21, 1.8) * mm});
            skLineSegment(sketch, "E167", {"start": v(5.21, 1.8) * mm, "end": v(11.56, 1.8) * mm});
            skLineSegment(sketch, "E168", {"start": v(11.56, 1.8) * mm, "end": v(11.56, -1.37) * mm});
            skLineSegment(sketch, "E169", {"start": v(5.21, -1.37) * mm, "end": v(11.56, -1.37) * mm});
            skSolve(sketch);
        }
        {
            var Q0;
            Q0=sQuery(id+"F10.wireOp",VERTEX,"E164.start");
            var Q1;
            Q1=sQuery(id+"F10.wireOp",VERTEX,"E163.start");
            var Q2;
            Q2=sQuery(id+"F11.wireOp",VERTEX,"E169.start");
            cPlane(context, id + "F12", {"entities" : qUnion([Q0, Q1, Q2]), "cplaneType" : CPlaneType.THREE_POINT, "offset" : 25.4 * mm, "width" : 152.4 * mm, "height" : 152.4 * mm});
        }
        {
            var Q0;
            Q0=qCreatedBy(id+"F12.planeOp",FACE);
            var sketch = newSketch(context, id + "F13", { "sketchPlane" : qUnion([Q0])});
            skPoint(sketch, "E170.0", {"position": v(-5.65, -5.08) * mm});
            skPoint(sketch, "E170.1", {"position": v(1.37, 174.87) * mm});
            skLineSegment(sketch, "E171", {"start": v(1.37, 174.87) * mm, "end": v(-5.65, -5.08) * mm});
            skSolve(sketch);
        }
        {
            var Q0;
            Q0 = qSketchRegion(id + "F10", true);
            var Q1;
            Q1=sQuery(id+"F13.wireOp",EDGE,"E171");
            sweep(context, id + "F14", {"operationType" : NewBodyOperationType.REMOVE, "profiles" : qUnion([Q0]), "path" : qUnion([Q1])});
        }
        {
            var Q0;
            Q0=makeQuery(id+"F0.imprint","IMPRINT",FACE,{"disambiguationData":[TD([[makeQuery(id+"F0.imprint","IMPRINT",EDGE,{"derivedFrom":sQuery(id+"F0.wireOp",EDGE,"E0")}),-1.0]])]});
            var sketch = newSketch(context, id + "F15", { "sketchPlane" : qUnion([Q0])});
            skLineSegment(sketch, "E172.bottom", {"start": v(91.52, -6.28) * mm, "end": v(88.34, -6.28) * mm});
            skLineSegment(sketch, "E172.top", {"start": v(91.52, -9.46) * mm, "end": v(88.34, -9.46) * mm});
            skLineSegment(sketch, "E172.left", {"start": v(91.52, -6.28) * mm, "end": v(91.52, -9.46) * mm});
            skLineSegment(sketch, "E172.right", {"start": v(88.34, -6.28) * mm, "end": v(88.34, -9.46) * mm});
            skSolve(sketch);
        }
        {
            var Q0;
            Q0=makeQuery(id+"F7.boolean.opBoolean","COPY",FACE,{"derivedFrom":makeQuery(id+"F7.opExtrude","SWEPT_FACE",FACE,{"disambiguationData":[OSD([sQuery(id+"F6.wireOp",EDGE,"E153.0.3.3")])]})});
            var sketch = newSketch(context, id + "F16", { "sketchPlane" : qUnion([Q0])});
            skLineSegment(sketch, "E173.bottom", {"start": v(40.74, -1.91) * mm, "end": v(43.91, -1.91) * mm});
            skLineSegment(sketch, "E173.top", {"start": v(40.74, -5.09) * mm, "end": v(43.91, -5.09) * mm});
            skLineSegment(sketch, "E173.left", {"start": v(40.74, -1.91) * mm, "end": v(40.74, -5.09) * mm});
            skLineSegment(sketch, "E173.right", {"start": v(43.91, -1.91) * mm, "end": v(43.91, -5.09) * mm});
            skSolve(sketch);
        }
        {
            var Q0;
            Q0 = qSketchRegion(id + "F15", true);
            var Q1;
            Q1 = qSketchRegion(id + "F16", true);
            loft(context, id + "F17", {"operationType" : NewBodyOperationType.REMOVE, "sheetProfilesArray" : [{ "sheetProfileEntities" : qUnion([Q0]) }, { "sheetProfileEntities" : qUnion([Q1]) }]});
        }
    });
